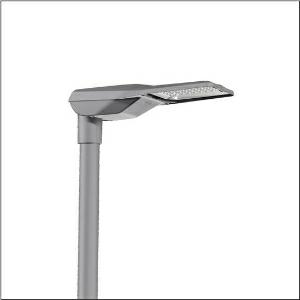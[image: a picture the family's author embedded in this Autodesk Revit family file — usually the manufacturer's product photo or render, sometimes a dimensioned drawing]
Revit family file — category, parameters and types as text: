
# Revit family: streetlight_sl_21_iq_mini___st0_8a_5xe2c31g08gb_0650
name_source: partatom
category: Lighting Fixtures
units: mm (PartAtom-declared; Revit-internal decimal feet)

## family parameters
Cut with Voids When Loaded = No
Host = Face
Light Source = No
Part Type = Normal
Room Calculation Point = No
Round Connector Dimension = Use Diameter
Shared = No

## types (1)
- --- (1 x LED, 5680 lm, 37.1 W, 3000K)
    Apparent Load = 37 VA
    CIE Flux Codes = 38 75 97 100 100
    Color Rendering = 70
    Color Temperature = 3000K
    Default Elevation = 1800 mm
    Description = Streetlight SL 21 iQ mini, mast luminaire, primary light control with lens, of PMMA, primary optical cover: cover, of toughened safety glass, transparent, light distribution: ST0.8a, light emission: direct distribution, primary light characteristic: asymmetric, installation type: post-top, side-entry, LED, High Power LED, rated luminous flux: 5.680lm, luminous efficacy: 153lm/W, light colour: 730, colour temperature: 3000K, control gear: iQ Street-Remote, control: Street-Remote, Auto-Match, Temp-Guard, Lumen-Switch, Night-Set, Smart-Wire, Light-Fading, Desk-Remote (wireless, voltage-free reading and setting of iQ features in the workshop via application-optimized NFC function/RFID function), optimised constant luminous flux control (CLO 2.0), pre-setting: linear dimming characteristic, mains connection: 220..240V, AC, 50/60Hz, start of lifetime: 37W, end of service life: 39W, reduction: 18W, luminaire housing, of diecast aluminium, powder-coated, Siteco® metallic grey (DB 702S), corrosivity category C5 mid according to DIN EN ISO 12944, please order mast flange separately, inclination adjustable: 0°, 5°, 10°, 15°, sealing non-destructively replaceable, multi-level sealing system, length: 628mm, width: 235mm, height: 110mm, mast flange for spigot size: 42mm (side-entry): 5XC10008XM4, 60/48mm (side-entry/post-top): 5XC10108XM2, 76/60mm (side-entry/post-top): 5XC10108XM1, mounting height: 4..8m, protection rating (complete): IP66, insulation class (complete): insulation class II (safety insulation), certification: CE, ENEC, ENEC+, VDE, impact resistance: IK10, permissible operating ambient temperature for outdoor applications: -40..+50°C, standard-compliant lighting for roads and squares, packaging unit: 1 piece

Light Distribution: ST0.8a
    Height = 110 mm
    Lamp = 1 x LED
    Lamp Light Flux = 5680 lm
    Lamp Power = 37.1 W
    Lamp count = 1
    Length = 625 mm
    Luminous efficacy = 153 lm/W
    Manufacturer = Siteco
    ModVariant = No
    Model = 5XE2C31G08GB
    Number of Poles = 1
    OnlyDefault = Yes
    Power Factor = 1
    Product Name = Streetlight SL 21 iQ mini | ST0.8a
    Product group = mast luminaire | pylon top
    ProductGroupID = 6100
    Protection Class = Protection class II
    Protection Degree = IP 66
    RLX_Detail_Level = 1
    RLX_Emergency_Light_Flux = 0 lm
    RLX_Emergency_Type = 0
    RLX_Emergency_Type_DB = No
    RlxData = <blob elided: 26373 chars, md5=94f418e8>
    Socket = socket
    Standby Power = 0 W
    System Light Flux = 5680 lm
    System Power = 37 W
    Type Comments = factory setting: luminous flux: 100 % | dim-lin: 254 | 385 mA
    Type Image = l_1003519.jpg
    URL = http://relux.com
    VarID = @adj_206979
    Voltage = 0 V
    Weight = 0.00 kg
    Width = 234 mm

## geometry (parser evidence)
native form markers: Blend x4, Sweep x9
no freeform markers — native parametric forms only
